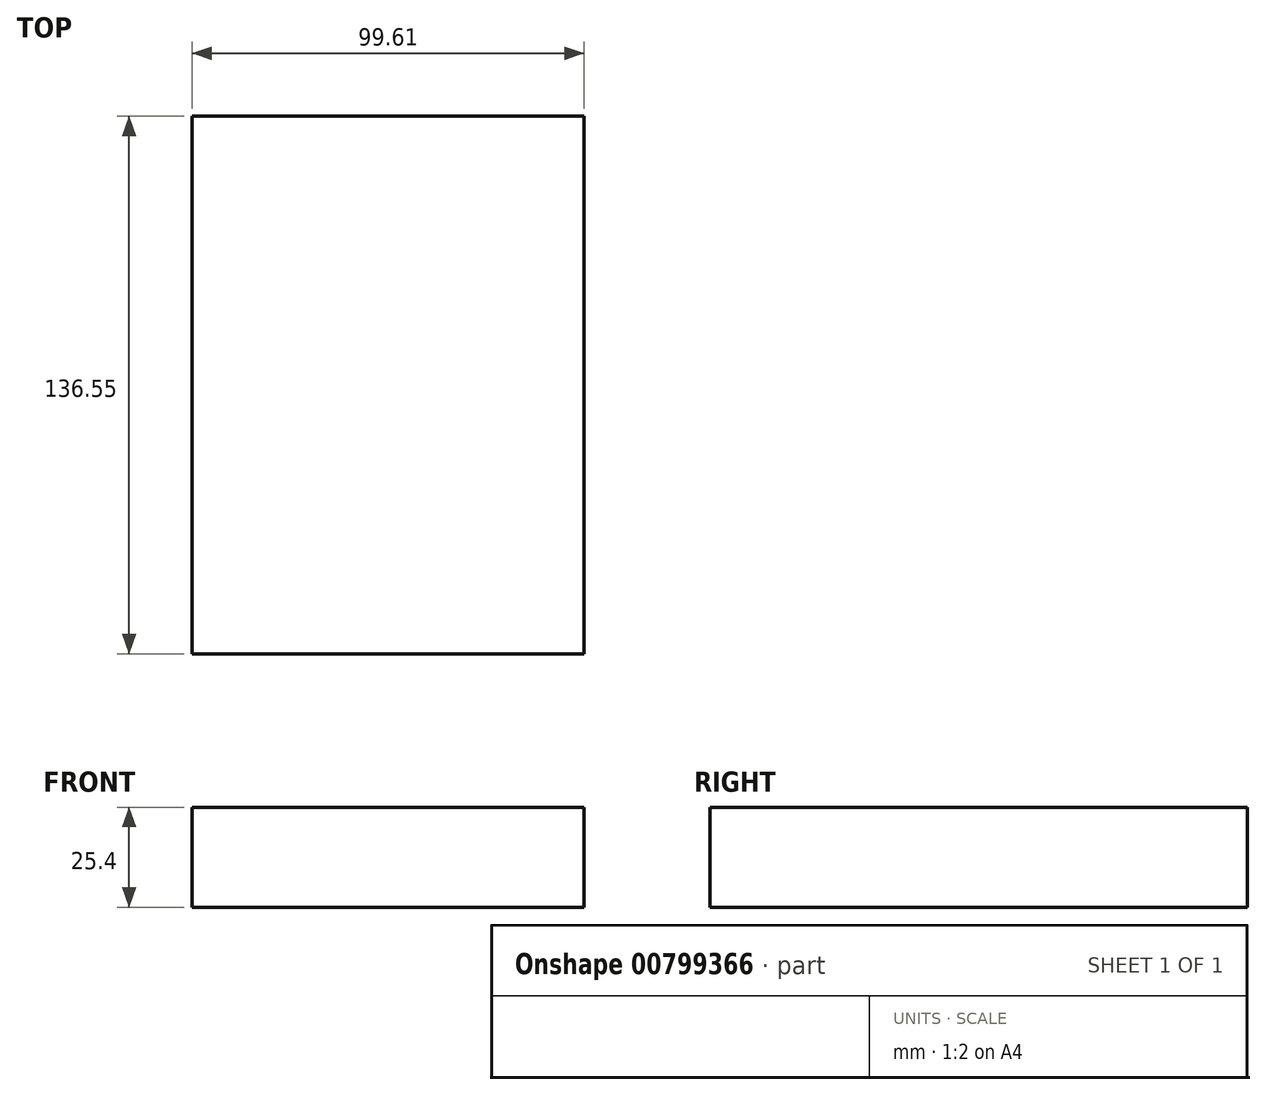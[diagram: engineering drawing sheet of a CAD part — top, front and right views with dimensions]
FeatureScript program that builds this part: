
annotation { "Feature Type Name" : "Feature", "Feature Type Description" : "" }
export const myFeature = defineFeature(function(context is Context, id is Id, definition is map)
    precondition{}
    {
        {
            var Q0;
            Q0=qCreatedBy(makeId("Top.planeOp"),FACE);
            var sketch = newSketch(context, id + "F0", { "sketchPlane" : qUnion([Q0])});
            skLineSegment(sketch, "E0.bottom", {"start": v(0, 0) * mm, "end": v(99.61, 0) * mm});
            skLineSegment(sketch, "E0.top", {"start": v(0, 136.55) * mm, "end": v(99.61, 136.55) * mm});
            skLineSegment(sketch, "E0.left", {"start": v(0, 0) * mm, "end": v(0, 136.55) * mm});
            skLineSegment(sketch, "E0.right", {"start": v(99.61, 0) * mm, "end": v(99.61, 136.55) * mm});
            skSolve(sketch);
        }
        {
            var Q0;
            Q0=makeQuery(id+"F0.imprint","IMPRINT",FACE,{"disambiguationData":[TD([[makeQuery(id+"F0.imprint","IMPRINT",EDGE,{"derivedFrom":sQuery(id+"F0.wireOp",EDGE,"E0.bottom")}),1.0]])]});
            extrude(context, id + "F1", {"entities" : qUnion([Q0]), "depth" : 25.4 * mm, "offsetDistance" : 25.4 * mm});
        }
    });
